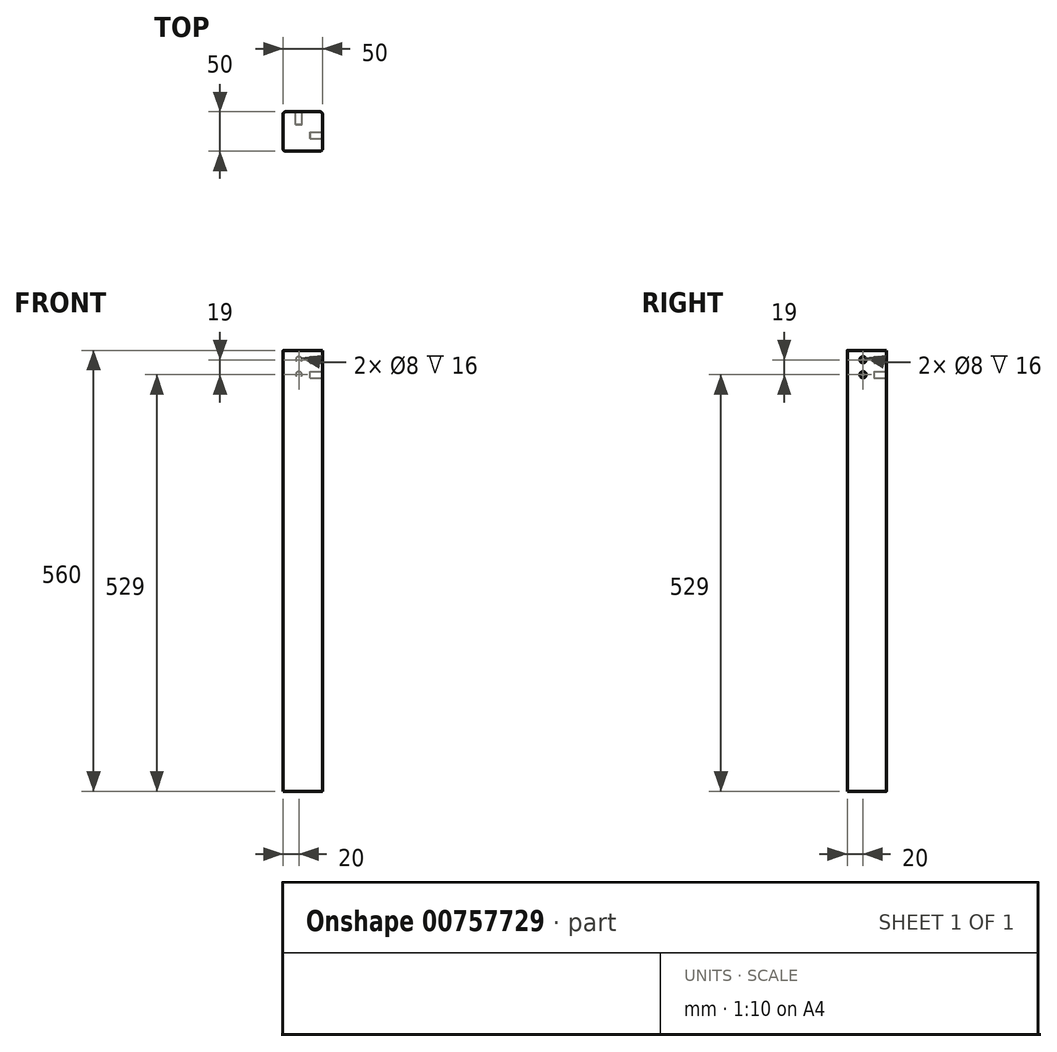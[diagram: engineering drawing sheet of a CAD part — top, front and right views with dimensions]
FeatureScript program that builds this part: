
annotation { "Feature Type Name" : "Feature", "Feature Type Description" : "" }
export const myFeature = defineFeature(function(context is Context, id is Id, definition is map)
    precondition{}
    {
        {
            var Q0;
            Q0=qCreatedBy(makeId("Top.planeOp"),FACE);
            var sketch = newSketch(context, id + "F0", { "sketchPlane" : qUnion([Q0])});
            skLineSegment(sketch, "E0.bottom", {"start": v(22, 25) * mm, "end": v(-22, 25) * mm});
            skLineSegment(sketch, "E0.top", {"start": v(22, -25) * mm, "end": v(-22, -25) * mm});
            skLineSegment(sketch, "E0.left", {"start": v(25, 22) * mm, "end": v(25, -22) * mm});
            skLineSegment(sketch, "E0.right", {"start": v(-25, 22) * mm, "end": v(-25, -22) * mm});
            skPoint(sketch, "E0.middle", {"position": v(0, 0) * mm});
            skPoint(sketch, "E1.visualSharp", {"position": v(-25, 25) * mm});
            skArc(sketch, "E1.filletArc", {"start": v(-22, 25) * mm, "mid": v(-24.12, 24.12) * mm, "end": v(-25, 22) * mm});
            skPoint(sketch, "E2.visualSharp", {"position": v(25, 25) * mm});
            skArc(sketch, "E2.filletArc", {"start": v(25, 22) * mm, "mid": v(24.12, 24.12) * mm, "end": v(22, 25) * mm});
            skPoint(sketch, "E3.visualSharp", {"position": v(25, -25) * mm});
            skArc(sketch, "E3.filletArc", {"start": v(22, -25) * mm, "mid": v(24.12, -24.12) * mm, "end": v(25, -22) * mm});
            skPoint(sketch, "E4.visualSharp", {"position": v(-25, -25) * mm});
            skArc(sketch, "E4.filletArc", {"start": v(-25, -22) * mm, "mid": v(-24.12, -24.12) * mm, "end": v(-22, -25) * mm});
            skSolve(sketch);
        }
        {
            var Q0;
            Q0=makeQuery(id+"F0.imprint","IMPRINT",FACE,{"disambiguationData":[TD([[makeQuery(id+"F0.imprint","IMPRINT",EDGE,{"derivedFrom":sQuery(id+"F0.wireOp",EDGE,"E0.bottom")}),1.0]])]});
            extrude(context, id + "F1", {"entities" : qUnion([Q0]), "oppositeDirection" : true, "depth" : 560 * mm, "offsetDistance" : 25 * mm});
        }
        {
            var Q0;
            Q0=makeQuery(id+"F1.opExtrude","SWEPT_FACE",FACE,{"disambiguationData":[OSD([sQuery(id+"F0.wireOp",EDGE,"E0.left")])]});
            var sketch = newSketch(context, id + "F2", { "sketchPlane" : qUnion([Q0])});
            skCircle(sketch, "E5", {"center": v(-5, -12) * mm, "radius": 4 * mm});
            skCircle(sketch, "E6", {"center": v(-5, -31) * mm, "radius": 4 * mm});
            skSolve(sketch);
        }
        {
            var Q0;
            Q0=makeQuery(id+"F1.opExtrude","SWEPT_FACE",FACE,{"disambiguationData":[OSD([sQuery(id+"F0.wireOp",EDGE,"E0.bottom")])]});
            var sketch = newSketch(context, id + "F3", { "sketchPlane" : qUnion([Q0])});
            skCircle(sketch, "E7", {"center": v(5, -12) * mm, "radius": 4 * mm});
            skCircle(sketch, "E8", {"center": v(5, -31) * mm, "radius": 4 * mm});
            skSolve(sketch);
        }
        {
            var Q0;
            Q0=makeQuery(id+"F2.imprint","IMPRINT",FACE,{"disambiguationData":[TD([[makeQuery(id+"F2.imprint","IMPRINT",EDGE,{"derivedFrom":sQuery(id+"F2.wireOp",EDGE,"E5")}),1.0]])]});
            var Q1;
            Q1=makeQuery(id+"F2.imprint","IMPRINT",FACE,{"disambiguationData":[TD([[makeQuery(id+"F2.imprint","IMPRINT",EDGE,{"derivedFrom":sQuery(id+"F2.wireOp",EDGE,"E6")}),1.0]])]});
            extrude(context, id + "F4", {"entities" : qUnion([Q0, Q1]), "operationType" : NewBodyOperationType.REMOVE, "oppositeDirection" : true, "depth" : 16 * mm, "offsetDistance" : 25 * mm});
        }
        {
            var Q0;
            Q0=makeQuery(id+"F3.imprint","IMPRINT",FACE,{"disambiguationData":[TD([[makeQuery(id+"F3.imprint","IMPRINT",EDGE,{"derivedFrom":sQuery(id+"F3.wireOp",EDGE,"E7")}),1.0]])]});
            var Q1;
            Q1=makeQuery(id+"F3.imprint","IMPRINT",FACE,{"disambiguationData":[TD([[makeQuery(id+"F3.imprint","IMPRINT",EDGE,{"derivedFrom":sQuery(id+"F3.wireOp",EDGE,"E8")}),1.0]])]});
            extrude(context, id + "F5", {"entities" : qUnion([Q0, Q1]), "operationType" : NewBodyOperationType.REMOVE, "oppositeDirection" : true, "depth" : 16 * mm, "offsetDistance" : 25 * mm});
        }
    });
